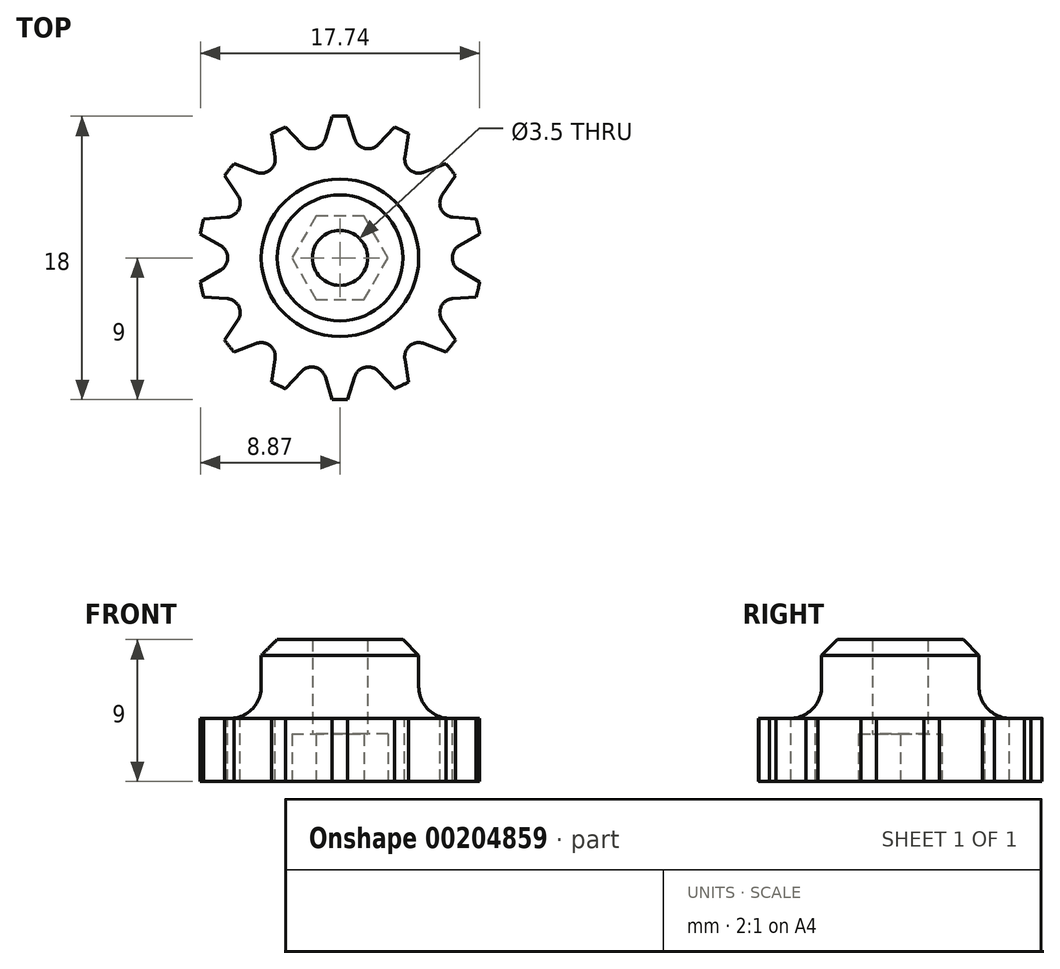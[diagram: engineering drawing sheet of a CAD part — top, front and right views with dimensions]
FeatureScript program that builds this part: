
annotation { "Feature Type Name" : "Feature", "Feature Type Description" : "" }
export const myFeature = defineFeature(function(context is Context, id is Id, definition is map)
    precondition{}
    {
        {
            var Q0;
            Q0=qCreatedBy(makeId("Front.planeOp"),FACE);
            var sketch = newSketch(context, id + "F0", { "sketchPlane" : qUnion([Q0])});
            skLineSegment(sketch, "E0", {"start": v(0, -6) * mm, "end": v(-9, -6) * mm});
            skLineSegment(sketch, "E1", {"start": v(0, -6) * mm, "end": v(0, 3) * mm});
            skLineSegment(sketch, "E2", {"start": v(0, 3) * mm, "end": v(-5, 3) * mm});
            skLineSegment(sketch, "E3", {"start": v(-5, 3) * mm, "end": v(-5, -2) * mm});
            skLineSegment(sketch, "E4", {"start": v(-9, -2) * mm, "end": v(-5, -2) * mm});
            skLineSegment(sketch, "E5", {"start": v(-9, -2) * mm, "end": v(-9, -6) * mm});
            skSolve(sketch);
        }
        {
            var Q0;
            Q0=makeQuery(id+"F0.imprint","IMPRINT",FACE,{"disambiguationData":[TD([[makeQuery(id+"F0.imprint","IMPRINT",EDGE,{"derivedFrom":sQuery(id+"F0.wireOp",EDGE,"E0")}),-1.0]])]});
            var Q1;
            Q1=sQuery(id+"F0.wireOp",EDGE,"E1");
            revolve(context, id + "F1", {"entities" : qUnion([Q0]), "axis" : qUnion([Q1]), "revolveType" : RevolveType.FULL});
        }
        {
            var Q0;
            Q0=qCreatedBy(makeId("Top.planeOp"),FACE);
            var sketch = newSketch(context, id + "F2", { "sketchPlane" : qUnion([Q0])});
            skCircle(sketch, "E6", {"center": v(0, 0) * mm, "radius": 1.75 * mm});
            skSolve(sketch);
        }
        {
            var Q0;
            Q0=makeQuery(id+"F2.imprint","IMPRINT",FACE,{"disambiguationData":[TD([[makeQuery(id+"F2.imprint","IMPRINT",EDGE,{"derivedFrom":sQuery(id+"F2.wireOp",EDGE,"E6")}),1.0]])]});
            extrude(context, id + "F3", {"entities" : qUnion([Q0]), "endBound" : BoundingType.SYMMETRIC, "depth" : 25 * mm});
        }
        {
            var Q0;
            Q0=makeQuery(id+"F3.opExtrude","SWEPT_BODY",BODY,{"disambiguationData":[OSD([sQuery(id+"F2.wireOp",EDGE,"E6")])]});
            var Q1;
            Q1=makeQuery(id+"F1.opRevolve","SWEPT_BODY",BODY,{"disambiguationData":[OSD([sQuery(id+"F0.wireOp",EDGE,"E0"),sQuery(id+"F0.wireOp",EDGE,"hmLDlmhl-fUHp-Yytk-PDIj-Sccdh0N3rT8E"),sQuery(id+"F0.wireOp",EDGE,"E1"),sQuery(id+"F0.wireOp",EDGE,"E2"),sQuery(id+"F0.wireOp",EDGE,"E3"),sQuery(id+"F0.wireOp",EDGE,"E4")])]});
            booleanBodies(context, id + "F4", {"operationType" : BooleanOperationType.SUBTRACTION, "tools" : qUnion([Q0]), "targets" : qUnion([Q1])});
        }
        {
            var Q0;
            Q0=makeQuery(id+"F1.opRevolve","SWEPT_EDGE",EDGE,{"disambiguationData":[OSD([sQuery(id+"F0.wireOp",EDGE,"E3"),sQuery(id+"F0.wireOp",EDGE,"E4")])]});
            fillet(context, id + "F5", {"entities" : qUnion([Q0]), "radius" : 2 * mm, "tangentPropagation" : true, "allowEdgeOverflow" : false});
        }
        {
            var Q0;
            Q0=qCreatedBy(makeId("Top.planeOp"),FACE);
            var sketch = newSketch(context, id + "F6", { "sketchPlane" : qUnion([Q0])});
            skLineSegment(sketch, "E7", {"start": v(-7.58, 0.78) * mm, "end": v(-10.5, 2.46) * mm});
            skLineSegment(sketch, "E8", {"start": v(-10.5, 2.46) * mm, "end": v(-10.5, -2.46) * mm});
            skLineSegment(sketch, "E9", {"start": v(-10.5, -2.46) * mm, "end": v(-7.58, -0.78) * mm});
            skLineSegment(sketch, "E10.1.0", {"start": v(-7.17, -2.59) * mm, "end": v(-10.53, -2.34) * mm});
            skLineSegment(sketch, "E10.1.1", {"start": v(-10.53, -2.34) * mm, "end": v(-8.4, -6.77) * mm});
            skLineSegment(sketch, "E10.1.2", {"start": v(-8.4, -6.77) * mm, "end": v(-6.5, -3.99) * mm});
            skLineSegment(sketch, "E10.2.0", {"start": v(-5.33, -5.44) * mm, "end": v(-8.47, -6.67) * mm});
            skLineSegment(sketch, "E10.2.1", {"start": v(-8.47, -6.67) * mm, "end": v(-4.62, -9.74) * mm});
            skLineSegment(sketch, "E10.2.2", {"start": v(-4.62, -9.74) * mm, "end": v(-4.12, -6.4) * mm});
            skLineSegment(sketch, "E10.3.0", {"start": v(-2.44, -7.22) * mm, "end": v(-4.74, -9.69) * mm});
            skLineSegment(sketch, "E10.3.1", {"start": v(-4.74, -9.69) * mm, "end": v(0.06, -10.78) * mm});
            skLineSegment(sketch, "E10.3.2", {"start": v(0.06, -10.78) * mm, "end": v(-0.93, -7.56) * mm});
            skLineSegment(sketch, "E10.4.0", {"start": v(0.93, -7.56) * mm, "end": v(-0.06, -10.78) * mm});
            skLineSegment(sketch, "E10.4.1", {"start": v(-0.06, -10.78) * mm, "end": v(4.74, -9.69) * mm});
            skLineSegment(sketch, "E10.4.2", {"start": v(4.74, -9.69) * mm, "end": v(2.44, -7.22) * mm});
            skLineSegment(sketch, "E10.5.0", {"start": v(4.12, -6.4) * mm, "end": v(4.62, -9.74) * mm});
            skLineSegment(sketch, "E10.5.1", {"start": v(4.62, -9.74) * mm, "end": v(8.47, -6.67) * mm});
            skLineSegment(sketch, "E10.5.2", {"start": v(8.47, -6.67) * mm, "end": v(5.33, -5.44) * mm});
            skLineSegment(sketch, "E10.6.0", {"start": v(6.5, -3.99) * mm, "end": v(8.4, -6.77) * mm});
            skLineSegment(sketch, "E10.6.1", {"start": v(8.4, -6.77) * mm, "end": v(10.53, -2.34) * mm});
            skLineSegment(sketch, "E10.6.2", {"start": v(10.53, -2.34) * mm, "end": v(7.17, -2.59) * mm});
            skLineSegment(sketch, "E10.7.0", {"start": v(7.58, -0.78) * mm, "end": v(10.5, -2.46) * mm});
            skLineSegment(sketch, "E10.7.1", {"start": v(10.5, -2.46) * mm, "end": v(10.5, 2.46) * mm});
            skLineSegment(sketch, "E10.7.2", {"start": v(10.5, 2.46) * mm, "end": v(7.58, 0.78) * mm});
            skLineSegment(sketch, "E10.8.0", {"start": v(7.17, 2.59) * mm, "end": v(10.53, 2.34) * mm});
            skLineSegment(sketch, "E10.8.1", {"start": v(10.53, 2.34) * mm, "end": v(8.4, 6.77) * mm});
            skLineSegment(sketch, "E10.8.2", {"start": v(8.4, 6.77) * mm, "end": v(6.5, 3.99) * mm});
            skLineSegment(sketch, "E10.9.0", {"start": v(5.33, 5.44) * mm, "end": v(8.47, 6.67) * mm});
            skLineSegment(sketch, "E10.9.1", {"start": v(8.47, 6.67) * mm, "end": v(4.62, 9.74) * mm});
            skLineSegment(sketch, "E10.9.2", {"start": v(4.62, 9.74) * mm, "end": v(4.12, 6.4) * mm});
            skLineSegment(sketch, "E10.10.0", {"start": v(2.44, 7.22) * mm, "end": v(4.74, 9.69) * mm});
            skLineSegment(sketch, "E10.10.1", {"start": v(4.74, 9.69) * mm, "end": v(-0.06, 10.78) * mm});
            skLineSegment(sketch, "E10.10.2", {"start": v(-0.06, 10.78) * mm, "end": v(0.93, 7.56) * mm});
            skLineSegment(sketch, "E10.11.0", {"start": v(-0.93, 7.56) * mm, "end": v(0.06, 10.78) * mm});
            skLineSegment(sketch, "E10.11.1", {"start": v(0.06, 10.78) * mm, "end": v(-4.74, 9.69) * mm});
            skLineSegment(sketch, "E10.11.2", {"start": v(-4.74, 9.69) * mm, "end": v(-2.44, 7.22) * mm});
            skLineSegment(sketch, "E10.12.0", {"start": v(-4.12, 6.4) * mm, "end": v(-4.62, 9.74) * mm});
            skLineSegment(sketch, "E10.12.1", {"start": v(-4.62, 9.74) * mm, "end": v(-8.47, 6.67) * mm});
            skLineSegment(sketch, "E10.12.2", {"start": v(-8.47, 6.67) * mm, "end": v(-5.33, 5.44) * mm});
            skLineSegment(sketch, "E10.13.0", {"start": v(-6.5, 3.99) * mm, "end": v(-8.4, 6.77) * mm});
            skLineSegment(sketch, "E10.13.1", {"start": v(-8.4, 6.77) * mm, "end": v(-10.53, 2.34) * mm});
            skLineSegment(sketch, "E10.13.2", {"start": v(-10.53, 2.34) * mm, "end": v(-7.17, 2.59) * mm});
            skPoint(sketch, "E10.center", {"position": v(0, 0) * mm});
            skPoint(sketch, "E11.visualSharp", {"position": v(-5.62, 2.7) * mm});
            skArc(sketch, "E11.filletArc", {"start": v(-7.17, 2.59) * mm, "mid": v(-6.43, 3.1) * mm, "end": v(-6.5, 3.99) * mm});
            skPoint(sketch, "E12.visualSharp", {"position": v(-3.89, 4.88) * mm});
            skArc(sketch, "E12.filletArc", {"start": v(-5.33, 5.44) * mm, "mid": v(-4.45, 5.58) * mm, "end": v(-4.12, 6.4) * mm});
            skPoint(sketch, "E13.visualSharp", {"position": v(-1.39, 6.08) * mm});
            skArc(sketch, "E13.filletArc", {"start": v(-2.44, 7.22) * mm, "mid": v(-1.59, 6.95) * mm, "end": v(-0.93, 7.56) * mm});
            skPoint(sketch, "E14.visualSharp", {"position": v(1.39, 6.08) * mm});
            skArc(sketch, "E14.filletArc", {"start": v(0.93, 7.56) * mm, "mid": v(1.59, 6.95) * mm, "end": v(2.44, 7.22) * mm});
            skPoint(sketch, "E15.visualSharp", {"position": v(3.89, 4.88) * mm});
            skArc(sketch, "E15.filletArc", {"start": v(4.12, 6.4) * mm, "mid": v(4.45, 5.58) * mm, "end": v(5.33, 5.44) * mm});
            skPoint(sketch, "E16.visualSharp", {"position": v(5.62, 2.7) * mm});
            skArc(sketch, "E16.filletArc", {"start": v(6.5, 3.99) * mm, "mid": v(6.43, 3.1) * mm, "end": v(7.17, 2.59) * mm});
            skPoint(sketch, "E17.visualSharp", {"position": v(6.24, 0) * mm});
            skArc(sketch, "E17.filletArc", {"start": v(7.58, 0.78) * mm, "mid": v(7.13, 0) * mm, "end": v(7.58, -0.78) * mm});
            skPoint(sketch, "E18.visualSharp", {"position": v(5.62, -2.7) * mm});
            skArc(sketch, "E18.filletArc", {"start": v(7.17, -2.59) * mm, "mid": v(6.43, -3.1) * mm, "end": v(6.5, -3.99) * mm});
            skPoint(sketch, "E19.visualSharp", {"position": v(3.89, -4.88) * mm});
            skArc(sketch, "E19.filletArc", {"start": v(5.33, -5.44) * mm, "mid": v(4.45, -5.58) * mm, "end": v(4.12, -6.4) * mm});
            skPoint(sketch, "E20.visualSharp", {"position": v(1.39, -6.08) * mm});
            skArc(sketch, "E20.filletArc", {"start": v(2.44, -7.22) * mm, "mid": v(1.59, -6.95) * mm, "end": v(0.93, -7.56) * mm});
            skPoint(sketch, "E21.visualSharp", {"position": v(-1.39, -6.08) * mm});
            skArc(sketch, "E21.filletArc", {"start": v(-0.93, -7.56) * mm, "mid": v(-1.59, -6.95) * mm, "end": v(-2.44, -7.22) * mm});
            skPoint(sketch, "E22.visualSharp", {"position": v(-3.89, -4.88) * mm});
            skArc(sketch, "E22.filletArc", {"start": v(-4.12, -6.4) * mm, "mid": v(-4.45, -5.58) * mm, "end": v(-5.33, -5.44) * mm});
            skPoint(sketch, "E23.visualSharp", {"position": v(-5.62, -2.7) * mm});
            skArc(sketch, "E23.filletArc", {"start": v(-6.5, -3.99) * mm, "mid": v(-6.43, -3.1) * mm, "end": v(-7.17, -2.59) * mm});
            skPoint(sketch, "E24.visualSharp", {"position": v(-6.24, 0) * mm});
            skArc(sketch, "E24.filletArc", {"start": v(-7.58, -0.78) * mm, "mid": v(-7.13, 0) * mm, "end": v(-7.58, 0.78) * mm});
            skSolve(sketch);
        }
        {
            var Q0;
            Q0 = qSketchRegion(id + "F6", true);
            extrude(context, id + "F7", {"entities" : qUnion([Q0]), "operationType" : NewBodyOperationType.REMOVE, "oppositeDirection" : true, "depth" : 10 * mm});
        }
        {
            var Q0;
            Q0=makeQuery(id+"F1.opRevolve","SWEPT_FACE",FACE,{"disambiguationData":[OSD([sQuery(id+"F0.wireOp",EDGE,"E0")])]});
            var sketch = newSketch(context, id + "F8", { "sketchPlane" : qUnion([Q0])});
            skCircle(sketch, "E25.cCircle", {"center": v(0, 0) * mm, "radius": 2.65 * mm, "construction": true});
            skLineSegment(sketch, "E25.0", {"start": v(1.53, -2.65) * mm, "end": v(-1.53, -2.65) * mm});
            skLineSegment(sketch, "E25.1", {"start": v(-1.53, -2.65) * mm, "end": v(-3.06, 0) * mm});
            skLineSegment(sketch, "E25.2", {"start": v(-3.06, 0) * mm, "end": v(-1.53, 2.65) * mm});
            skLineSegment(sketch, "E25.3", {"start": v(-1.53, 2.65) * mm, "end": v(1.53, 2.65) * mm});
            skLineSegment(sketch, "E25.4", {"start": v(1.53, 2.65) * mm, "end": v(3.06, 0) * mm});
            skLineSegment(sketch, "E25.5", {"start": v(3.06, 0) * mm, "end": v(1.53, -2.65) * mm});
            skPoint(sketch, "E25.0.midPoint", {"position": v(0, -2.65) * mm});
            skSolve(sketch);
        }
        {
            var Q0;
            Q0=makeQuery(id+"F8.imprint","IMPRINT",FACE,{"disambiguationData":[TD([[makeQuery(id+"F8.imprint","IMPRINT",EDGE,{"derivedFrom":sQuery(id+"F8.wireOp",EDGE,"E25.0")}),-1.0]])]});
            extrude(context, id + "F9", {"entities" : qUnion([Q0]), "operationType" : NewBodyOperationType.REMOVE, "oppositeDirection" : true, "depth" : 3 * mm});
        }
        {
            var Q0;
            Q0=makeQuery(id+"F1.opRevolve","SWEPT_EDGE",EDGE,{"disambiguationData":[OSD([sQuery(id+"F0.wireOp",EDGE,"E2"),sQuery(id+"F0.wireOp",EDGE,"E3")])]});
            chamfer(context, id + "F10", {"entities" : qUnion([Q0]), "width" : 1 * mm, "tangentPropagation" : true});
        }
    });
